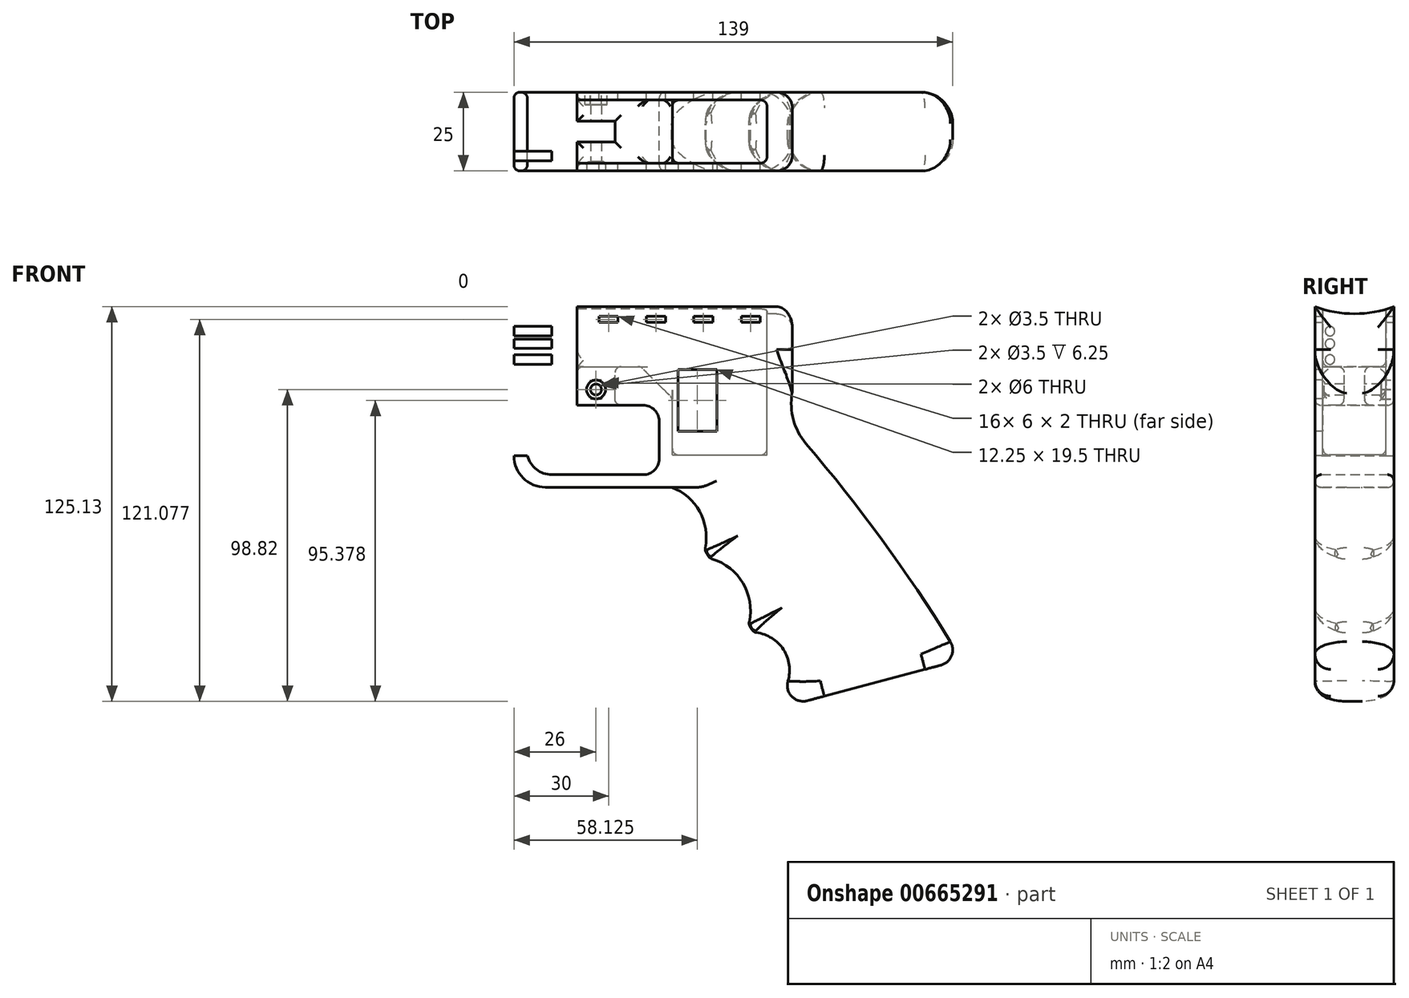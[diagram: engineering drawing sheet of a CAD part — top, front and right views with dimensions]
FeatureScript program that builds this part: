
annotation { "Feature Type Name" : "Feature", "Feature Type Description" : "" }
export const myFeature = defineFeature(function(context is Context, id is Id, definition is map)
    precondition{}
    {
        {
            assignVariable(context, id + "F0", {"name" : "TotalThickness", "anyValue" : 25});
        }
        {
            var Q0;
            Q0=qCreatedBy(makeId("Front.planeOp"),FACE);
            var sketch = newSketch(context, id + "F1", { "sketchPlane" : qUnion([Q0])});
            skLineSegment(sketch, "E0.top", {"start": v(-15, -15) * mm, "end": v(25, -15) * mm});
            skLineSegment(sketch, "E0.left", {"start": v(-25, 10) * mm, "end": v(-25, -5) * mm});
            skPoint(sketch, "E0.middle", {"position": v(0, 0) * mm});
            skLineSegment(sketch, "E1.top", {"start": v(25, 45.26) * mm, "end": v(-25, 45.26) * mm});
            skLineSegment(sketch, "E1.right", {"start": v(-25, 15) * mm, "end": v(-25, 45.26) * mm});
            skPoint(sketch, "E2.visualSharp", {"position": v(-25, -15) * mm});
            skArc(sketch, "E2.filletArc", {"start": v(-25, -5) * mm, "mid": v(-22.07, -12.07) * mm, "end": v(-15, -15) * mm});
            skLineSegment(sketch, "E3.bottom", {"start": v(-21, 11) * mm, "end": v(16, 11) * mm});
            skLineSegment(sketch, "E3.top", {"start": v(-13, -11) * mm, "end": v(16, -11) * mm});
            skLineSegment(sketch, "E3.left", {"start": v(-21, 11) * mm, "end": v(-21, -3) * mm});
            skLineSegment(sketch, "E3.right", {"start": v(21, 6) * mm, "end": v(21, -6) * mm});
            skPoint(sketch, "E4.visualSharp", {"position": v(-21, -11) * mm});
            skArc(sketch, "E4.filletArc", {"start": v(-21, -3) * mm, "mid": v(-18.66, -8.66) * mm, "end": v(-13, -11) * mm});
            skLineSegment(sketch, "E5", {"start": v(-25, 15) * mm, "end": v(-25, 10) * mm});
            skArc(sketch, "E6", {"start": v(60.37, -79.5) * mm, "mid": v(61, -67.48) * mm, "end": v(50.87, -60.96) * mm});
            skLineSegment(sketch, "E7", {"start": v(62.15, -84.17) * mm, "end": v(116.75, -69.64) * mm});
            skArc(sketch, "E8", {"start": v(115.2, -67.07) * mm, "mid": v(92.7, -33.16) * mm, "end": v(67.54, -1.2) * mm});
            skPoint(sketch, "E9.visualSharp", {"position": v(63.17, 15.26) * mm});
            skArc(sketch, "E10", {"start": v(35.45, -34.94) * mm, "mid": v(34, -23) * mm, "end": v(25, -15) * mm});
            skLineSegment(sketch, "E11", {"start": v(35.45, -34.94) * mm, "end": v(37, -37.5) * mm});
            skLineSegment(sketch, "E12", {"start": v(50.87, -60.96) * mm, "end": v(49.35, -58.38) * mm});
            skPoint(sketch, "E13", {"position": v(49.35, -58.38) * mm});
            skArc(sketch, "E14", {"start": v(49.35, -58.38) * mm, "mid": v(47.56, -45.35) * mm, "end": v(37, -37.5) * mm});
            skLineSegment(sketch, "E15", {"start": v(60.37, -79.5) * mm, "end": v(62.15, -84.17) * mm});
            skLineSegment(sketch, "E16", {"start": v(115.2, -67.07) * mm, "end": v(116.75, -69.64) * mm});
            skLineSegment(sketch, "E17.bottom", {"start": v(25, 45.26) * mm, "end": v(63.17, 45.26) * mm});
            skLineSegment(sketch, "E17.right", {"start": v(63.17, 45.26) * mm, "end": v(63.17, 15.26) * mm});
            skLineSegment(sketch, "E18.bottom", {"start": v(-13, 39.26) * mm, "end": v(-7, 39.26) * mm});
            skLineSegment(sketch, "E18.top", {"start": v(-13, 37.26) * mm, "end": v(-7, 37.26) * mm});
            skLineSegment(sketch, "E18.left", {"start": v(-13, 39.26) * mm, "end": v(-13, 37.26) * mm});
            skLineSegment(sketch, "E18.right", {"start": v(-7, 39.26) * mm, "end": v(-7, 37.26) * mm});
            skLineSegment(sketch, "E19.1.0.0", {"start": v(2, 37.26) * mm, "end": v(8, 37.26) * mm});
            skLineSegment(sketch, "E19.1.0.1", {"start": v(8, 39.26) * mm, "end": v(8, 37.26) * mm});
            skLineSegment(sketch, "E19.1.0.2", {"start": v(2, 39.26) * mm, "end": v(8, 39.26) * mm});
            skLineSegment(sketch, "E19.1.0.3", {"start": v(2, 39.26) * mm, "end": v(2, 37.26) * mm});
            skLineSegment(sketch, "E19.2.0.0", {"start": v(17, 37.26) * mm, "end": v(23, 37.26) * mm});
            skLineSegment(sketch, "E19.2.0.1", {"start": v(23, 39.26) * mm, "end": v(23, 37.26) * mm});
            skLineSegment(sketch, "E19.2.0.2", {"start": v(17, 39.26) * mm, "end": v(23, 39.26) * mm});
            skLineSegment(sketch, "E19.2.0.3", {"start": v(17, 39.26) * mm, "end": v(17, 37.26) * mm});
            skLineSegment(sketch, "E19.3.0.0", {"start": v(32, 37.26) * mm, "end": v(38, 37.26) * mm});
            skLineSegment(sketch, "E19.3.0.1", {"start": v(38, 39.26) * mm, "end": v(38, 37.26) * mm});
            skLineSegment(sketch, "E19.3.0.2", {"start": v(32, 39.26) * mm, "end": v(38, 39.26) * mm});
            skLineSegment(sketch, "E19.3.0.3", {"start": v(32, 39.26) * mm, "end": v(32, 37.26) * mm});
            skLineSegment(sketch, "E19.4.0.0", {"start": v(47, 37.26) * mm, "end": v(53, 37.26) * mm});
            skLineSegment(sketch, "E19.4.0.1", {"start": v(53, 39.26) * mm, "end": v(53, 37.26) * mm});
            skLineSegment(sketch, "E19.4.0.2", {"start": v(47, 39.26) * mm, "end": v(53, 39.26) * mm});
            skLineSegment(sketch, "E19.4.0.3", {"start": v(47, 39.26) * mm, "end": v(47, 37.26) * mm});
            skLineSegment(sketch, "E19.direction1", {"start": v(-13, 37.26) * mm, "end": v(2, 37.26) * mm, "construction": true});
            skArc(sketch, "E20", {"start": v(63.17, 15.26) * mm, "mid": v(63.52, 6.55) * mm, "end": v(67.54, -1.2) * mm});
            skPoint(sketch, "E21.visualSharp", {"position": v(21, 11) * mm});
            skArc(sketch, "E21.filletArc", {"start": v(21, 6) * mm, "mid": v(19.54, 9.54) * mm, "end": v(16, 11) * mm});
            skPoint(sketch, "E22.visualSharp", {"position": v(21, -11) * mm});
            skArc(sketch, "E22.filletArc", {"start": v(16, -11) * mm, "mid": v(19.54, -9.54) * mm, "end": v(21, -6) * mm});
            skSolve(sketch);
        }
        {
            var Q0;
            Q0=makeQuery(id+"F1.imprint","IMPRINT",FACE,{"disambiguationData":[TD([[makeQuery(id+"F1.imprint","IMPRINT",EDGE,{"derivedFrom":sQuery(id+"F1.wireOp",EDGE,"E0.top")}),1.0]])]});
            extrude(context, id + "F2", {"entities" : qUnion([Q0]), "depth" : (getVariable(context, 'TotalThickness')) * mm});
        }
        {
            var Q0;
            Q0=makeQuery(id+"FijhAChJVIiYrHk_1.boolean.opBoolean","MERGE",FACE,{"derivedFrom":[makeQuery(id+"F2.opExtrude","SWEPT_FACE",FACE,{"disambiguationData":[OSD([sQuery(id+"F1.wireOp",EDGE,"E1.top")])]}),makeQuery(id+"FijhAChJVIiYrHk_1.opExtrude","CAP_FACE",FACE,{"disambiguationData":[OSD([sQuery(id+"FPGrgiwVji8RH30_1.wireOp",EDGE,"540a66ce-eadd-4f73-87a4-8e37d69b1e98")])],"isStart":false})]});
            var sketch = newSketch(context, id + "F3", { "sketchPlane" : qUnion([Q0])});
            skLineSegment(sketch, "E23.bottom", {"start": v(-13, -2.5) * mm, "end": v(55.17, -2.5) * mm});
            skLineSegment(sketch, "E23.top", {"start": v(-13, -22.5) * mm, "end": v(55.17, -22.5) * mm});
            skLineSegment(sketch, "E23.left", {"start": v(-13, -2.5) * mm, "end": v(-13, -22.5) * mm});
            skLineSegment(sketch, "E23.right", {"start": v(55.17, -2.5) * mm, "end": v(55.17, -22.5) * mm});
            skLineSegment(sketch, "E24", {"start": v(25.17, -2.5) * mm, "end": v(25.17, -22.5) * mm});
            skSolve(sketch);
        }
        {
            var Q0;
            {var subQ0=sQuery(id+"F3.wireOp",EDGE,"E23.right");Q0=makeQuery(id+"F3.imprint","IMPRINT",FACE,{"disambiguationData":[TD([[makeQuery(id+"F3.imprint","IMPRINT",EDGE,{"derivedFrom":subQ0}),-1.0]])]});}
            extrude(context, id + "F4", {"entities" : qUnion([Q0]), "operationType" : NewBodyOperationType.REMOVE, "oppositeDirection" : true, "depth" : 50 * mm});
        }
        {
            var Q0;
            Q0=makeQuery(id+"F3.imprint","IMPRINT",FACE,{"disambiguationData":[TD([[makeQuery(id+"F3.imprint","IMPRINT",EDGE,{"derivedFrom":sQuery(id+"F3.wireOp",EDGE,"E23.bottom")}),-1.0]])]});
            extrude(context, id + "F5", {"entities" : qUnion([Q0]), "operationType" : NewBodyOperationType.REMOVE, "oppositeDirection" : true, "depth" : 22 * mm});
        }
        {
            var Q0;
            Q0=makeQuery(id+"F5.boolean.opBoolean","INTERSECT",EDGE,{"derivedFrom":[makeQuery(id+"F4.boolean.opBoolean","COPY",FACE,{"derivedFrom":makeQuery(id+"F4.opExtrude","SWEPT_FACE",FACE,{"disambiguationData":[OSD([sQuery(id+"F3.wireOp",EDGE,"E24")])]})}),makeQuery(id+"F5.opExtrude","CAP_FACE",FACE,{"disambiguationData":[OSD([sQuery(id+"F3.wireOp",EDGE,"E23.bottom"),sQuery(id+"F3.wireOp",EDGE,"E23.top"),sQuery(id+"F3.wireOp",EDGE,"E23.left"),sQuery(id+"F3.wireOp",EDGE,"E23.right")])],"isStart":false})]});
            chamfer(context, id + "F6", {"entities" : qUnion([Q0]), "width" : 10 * mm, "tangentPropagation" : true});
        }
        {
            var Q0;
            Q0=makeQuery(id+"F2.opExtrude","SWEPT_FACE",FACE,{"disambiguationData":[OSD([sQuery(id+"F1.wireOp",EDGE,"E1.right")])]});
            var sketch = newSketch(context, id + "F7", { "sketchPlane" : qUnion([Q0])});
            skLineSegment(sketch, "E25.bottom", {"start": v(9.25, 18.5) * mm, "end": v(15.75, 18.5) * mm});
            skLineSegment(sketch, "E25.top", {"start": v(9.25, 48.5) * mm, "end": v(15.75, 48.5) * mm});
            skLineSegment(sketch, "E25.left", {"start": v(9.25, 18.5) * mm, "end": v(9.25, 48.5) * mm});
            skLineSegment(sketch, "E25.right", {"start": v(15.75, 18.5) * mm, "end": v(15.75, 48.5) * mm});
            skPoint(sketch, "E25.middle", {"position": v(12.5, 33.5) * mm});
            skSolve(sketch);
        }
        {
            var Q0;
            Q0=makeQuery(id+"F7.imprint","IMPRINT",FACE,{"disambiguationData":[TD([[makeQuery(id+"F7.imprint","IMPRINT",EDGE,{"derivedFrom":sQuery(id+"F7.wireOp",EDGE,"E25.bottom")}),1.0]])]});
            extrude(context, id + "F8", {"entities" : qUnion([Q0]), "operationType" : NewBodyOperationType.REMOVE, "oppositeDirection" : true, "depth" : 20 * mm, "offsetDistance" : 25 * mm});
        }
        {
            var Q0;
            Q0=makeQuery(id+"F5.boolean.opBoolean","COPY",FACE,{"derivedFrom":makeQuery(id+"F5.opExtrude","CAP_FACE",FACE,{"disambiguationData":[OSD([sQuery(id+"F3.wireOp",EDGE,"E23.bottom"),sQuery(id+"F3.wireOp",EDGE,"E23.top"),sQuery(id+"F3.wireOp",EDGE,"E23.left"),sQuery(id+"F3.wireOp",EDGE,"E23.right")])],"isStart":false})});
            var sketch = newSketch(context, id + "F9", { "sketchPlane" : qUnion([Q0])});
            skLineSegment(sketch, "E26.bottom", {"start": v(-5, -9.25) * mm, "end": v(7, -9.25) * mm});
            skLineSegment(sketch, "E26.top", {"start": v(-5, -15.75) * mm, "end": v(7, -15.75) * mm});
            skLineSegment(sketch, "E26.right", {"start": v(7, -9.25) * mm, "end": v(7, -15.75) * mm});
            skLineSegment(sketch, "E27", {"start": v(-5, -9.25) * mm, "end": v(-5, -15.75) * mm});
            skPoint(sketch, "E28", {"position": v(-5, -12.5) * mm});
            skSolve(sketch);
        }
        {
            var Q0;
            Q0=makeQuery(id+"FNvPxtAVWz8euOJ_1.opFillet","SPLIT",FACE,{"disambiguationData":[OD(1.0)],"derivedFrom":makeQuery(id+"F2.opExtrude","CAP_FACE",FACE,{"disambiguationData":[OSD([sQuery(id+"F1.wireOp",EDGE,"E0.bottom"),sQuery(id+"F1.wireOp",EDGE,"E0.top"),sQuery(id+"F1.wireOp",EDGE,"E0.left"),sQuery(id+"F1.wireOp",EDGE,"E0.right"),sQuery(id+"F1.wireOp",EDGE,"E1.bottom"),sQuery(id+"F1.wireOp",EDGE,"E1.top"),sQuery(id+"F1.wireOp",EDGE,"E1.left"),sQuery(id+"F1.wireOp",EDGE,"E1.right"),sQuery(id+"F1.wireOp",EDGE,"E2.filletArc"),sQuery(id+"F1.wireOp",EDGE,"20bca58f-3b4b-4199-85f8-e5d00a776496.filletArc"),sQuery(id+"F1.wireOp",EDGE,"E3.bottom"),sQuery(id+"F1.wireOp",EDGE,"E3.top"),sQuery(id+"F1.wireOp",EDGE,"E3.left"),sQuery(id+"F1.wireOp",EDGE,"E3.right"),sQuery(id+"F1.wireOp",EDGE,"E4.filletArc")])],"isStart":false})});
            var sketch = newSketch(context, id + "F10", { "sketchPlane" : qUnion([Q0])});
            skCircle(sketch, "E29", {"center": v(1, 16) * mm, "radius": 1.75 * mm});
            skCircle(sketch, "E30", {"center": v(1, 16) * mm, "radius": 3 * mm});
            skSolve(sketch);
        }
        {
            var Q0;
            Q0=makeQuery(id+"F10.imprint","IMPRINT",FACE,{"disambiguationData":[TD([[makeQuery(id+"F10.imprint","IMPRINT",EDGE,{"derivedFrom":sQuery(id+"F10.wireOp",EDGE,"E29")}),1.0]])]});
            extrude(context, id + "F11", {"entities" : qUnion([Q0]), "operationType" : NewBodyOperationType.REMOVE, "oppositeDirection" : true, "depth" : (getVariable(context, 'TotalThickness')) * mm});
        }
        {
            var Q0;
            Q0=makeQuery(id+"F10.imprint","IMPRINT",FACE,{"disambiguationData":[TD([[makeQuery(id+"F10.imprint","IMPRINT",EDGE,{"derivedFrom":sQuery(id+"F10.wireOp",EDGE,"E29")}),-1.0]])]});
            extrude(context, id + "F12", {"entities" : qUnion([Q0]), "operationType" : NewBodyOperationType.REMOVE, "oppositeDirection" : true, "depth" : 3 * mm});
        }
        {
            var Q0;
            Q0=makeQuery(id+"F12.boolean.opBoolean","COPY",EDGE,{"derivedFrom":makeQuery(id+"F12.opExtrude","CAP_EDGE",EDGE,{"disambiguationData":[OSD([sQuery(id+"F10.wireOp",EDGE,"E30")])],"isStart":false})});
            var Q1;
            Q1=makeQuery(id+"F12.boolean.opBoolean","COPY",EDGE,{"derivedFrom":makeQuery(id+"F12.opExtrude","CAP_EDGE",EDGE,{"disambiguationData":[OSD([sQuery(id+"F10.wireOp",EDGE,"E30")])],"isStart":true})});
            fillet(context, id + "F13", {"entities" : qUnion([Q0, Q1]), "radius" : 1 * mm, "tangentPropagation" : true, "allowEdgeOverflow" : false});
        }
        {
            var Q0;
            Q0=makeQuery(id+"FNvPxtAVWz8euOJ_1.opFillet","SPLIT",FACE,{"disambiguationData":[OD(0.0)],"derivedFrom":makeQuery(id+"F2.opExtrude","CAP_FACE",FACE,{"disambiguationData":[OSD([sQuery(id+"F1.wireOp",EDGE,"E0.bottom"),sQuery(id+"F1.wireOp",EDGE,"E0.top"),sQuery(id+"F1.wireOp",EDGE,"E0.left"),sQuery(id+"F1.wireOp",EDGE,"E0.right"),sQuery(id+"F1.wireOp",EDGE,"E1.top"),sQuery(id+"F1.wireOp",EDGE,"E1.left"),sQuery(id+"F1.wireOp",EDGE,"E1.right"),sQuery(id+"F1.wireOp",EDGE,"E2.filletArc"),sQuery(id+"F1.wireOp",EDGE,"20bca58f-3b4b-4199-85f8-e5d00a776496.filletArc"),sQuery(id+"F1.wireOp",EDGE,"E3.bottom"),sQuery(id+"F1.wireOp",EDGE,"E3.top"),sQuery(id+"F1.wireOp",EDGE,"E3.left"),sQuery(id+"F1.wireOp",EDGE,"E3.right"),sQuery(id+"F1.wireOp",EDGE,"E4.filletArc")])],"isStart":true})});
            var sketch = newSketch(context, id + "F14", { "sketchPlane" : qUnion([Q0])});
            skCircle(sketch, "E31.cCircle", {"center": v(-1, 16) * mm, "radius": 3 * mm, "construction": true});
            skLineSegment(sketch, "E31.0", {"start": v(-4.46, 15.93) * mm, "end": v(-2.8, 18.96) * mm});
            skLineSegment(sketch, "E31.1", {"start": v(-2.8, 18.96) * mm, "end": v(0.67, 19.03) * mm});
            skLineSegment(sketch, "E31.2", {"start": v(0.67, 19.03) * mm, "end": v(2.46, 16.07) * mm});
            skLineSegment(sketch, "E31.3", {"start": v(2.46, 16.07) * mm, "end": v(0.8, 13.04) * mm});
            skLineSegment(sketch, "E31.4", {"start": v(0.8, 13.04) * mm, "end": v(-2.67, 12.97) * mm});
            skLineSegment(sketch, "E31.5", {"start": v(-2.67, 12.97) * mm, "end": v(-4.46, 15.93) * mm});
            skPoint(sketch, "E31.0.midPoint", {"position": v(-3.63, 17.45) * mm});
            skSolve(sketch);
        }
        {
            var Q0;
            Q0=makeQuery(id+"F14.imprint","IMPRINT",FACE,{"disambiguationData":[TD([[makeQuery(id+"F14.imprint","IMPRINT",EDGE,{"derivedFrom":sQuery(id+"F14.wireOp",EDGE,"E31.0")}),-1.0]])]});
            extrude(context, id + "F15", {"entities" : qUnion([Q0]), "operationType" : NewBodyOperationType.REMOVE, "oppositeDirection" : true, "depth" : 4 * mm});
        }
        {
            var Q0;
            Q0=qCreatedBy(makeId("Right.planeOp"),FACE);
            var sketch = newSketch(context, id + "F16", { "sketchPlane" : qUnion([Q0])});
            skArc(sketch, "E32", {"start": v(-37.25, 50.25) * mm, "mid": v(-12.5, 40) * mm, "end": v(12.25, 50.25) * mm});
            skLineSegment(sketch, "E33", {"start": v(-12.5, 75) * mm, "end": v(-37.25, 50.25) * mm});
            skLineSegment(sketch, "E34", {"start": v(-12.5, 75) * mm, "end": v(12.25, 50.25) * mm});
            skLineSegment(sketch, "E35", {"start": v(-12.5, 75) * mm, "end": v(-12.5, 46.26) * mm});
            skArc(sketch, "E36", {"start": v(-35.48, 52.02) * mm, "mid": v(-12.5, 42.5) * mm, "end": v(10.48, 52.02) * mm});
            skSolve(sketch);
        }
        {
            var Q0;
            {var subQ0=sQuery(id+"F16.wireOp",EDGE,"E32");Q0=makeQuery(id+"F16.imprint","IMPRINT",FACE,{"disambiguationData":[TD([[makeQuery(id+"F16.imprint","IMPRINT",EDGE,{"derivedFrom":subQ0}),1.0]])]});}
            var Q1;
            {var subQ3=sQuery(id+"F16.wireOp",EDGE,"E36");Q1=makeQuery(id+"F16.imprint","IMPRINT",FACE,{"disambiguationData":[TD([[makeQuery(id+"F16.imprint","IMPRINT",EDGE,{"derivedFrom":subQ3}),1.0]])]});}
            extrude(context, id + "F17", {"entities" : qUnion([Q0, Q1]), "operationType" : NewBodyOperationType.REMOVE, "depth" : 70 * mm, "hasSecondDirection" : true, "secondDirectionOppositeDirection" : true, "secondDirectionDepth" : 25 * mm});
        }
        {
            var Q0;
            Q0=makeQuery(id+"F2.opExtrude","SWEPT_FACE",FACE,{"disambiguationData":[OSD([sQuery(id+"F1.wireOp",EDGE,"E0.left"),sQuery(id+"F1.wireOp",EDGE,"E1.right"),sQuery(id+"F1.wireOp",EDGE,"E5")])]});
            var sketch = newSketch(context, id + "F18", { "sketchPlane" : qUnion([Q0])});
            skCircle(sketch, "E37", {"center": v(4.75, 34.5) * mm, "radius": 1.5 * mm});
            skCircle(sketch, "E38", {"center": v(4.75, 30.5) * mm, "radius": 1.5 * mm});
            skCircle(sketch, "E39", {"center": v(4.75, 25.5) * mm, "radius": 1.5 * mm});
            skLineSegment(sketch, "E40", {"start": v(12.5, 18.5) * mm, "end": v(12.5, 39.93) * mm, "construction": true});
            skPoint(sketch, "E40.endSnap0", {"position": v(12.5, 18.5) * mm});
            skCircle(sketch, "E41.MirrorC", {"center": v(20.25, 34.5) * mm, "radius": 1.5 * mm});
            skCircle(sketch, "E42.MirrorC", {"center": v(20.25, 30.5) * mm, "radius": 1.5 * mm});
            skCircle(sketch, "E43.MirrorC", {"center": v(20.25, 25.5) * mm, "radius": 1.5 * mm});
            skSolve(sketch);
        }
        {
            var Q0;
            Q0=makeQuery(id+"F18.imprint","IMPRINT",FACE,{"disambiguationData":[TD([[makeQuery(id+"F18.imprint","IMPRINT",EDGE,{"derivedFrom":sQuery(id+"F18.wireOp",EDGE,"E37")}),1.0]])]});
            var Q1;
            Q1=makeQuery(id+"F18.imprint","IMPRINT",FACE,{"disambiguationData":[TD([[makeQuery(id+"F18.imprint","IMPRINT",EDGE,{"derivedFrom":sQuery(id+"F18.wireOp",EDGE,"E38")}),1.0]])]});
            var Q2;
            Q2=makeQuery(id+"F18.imprint","IMPRINT",FACE,{"disambiguationData":[TD([[makeQuery(id+"F18.imprint","IMPRINT",EDGE,{"derivedFrom":sQuery(id+"F18.wireOp",EDGE,"E39")}),1.0]])]});
            var Q3;
            Q3=makeQuery(id+"F18.imprint","IMPRINT",FACE,{"disambiguationData":[TD([[makeQuery(id+"F18.imprint","IMPRINT",EDGE,{"derivedFrom":sQuery(id+"F18.wireOp",EDGE,"E38")}),1.0]])]});
            var Q4;
            Q4=makeQuery(id+"F18.imprint","IMPRINT",FACE,{"disambiguationData":[TD([[makeQuery(id+"F18.imprint","IMPRINT",EDGE,{"derivedFrom":sQuery(id+"F18.wireOp",EDGE,"E43.MirrorC")}),-1.0]])]});
            var Q5;
            Q5=makeQuery(id+"F18.imprint","IMPRINT",FACE,{"disambiguationData":[TD([[makeQuery(id+"F18.imprint","IMPRINT",EDGE,{"derivedFrom":sQuery(id+"F18.wireOp",EDGE,"E42.MirrorC")}),-1.0]])]});
            var Q6;
            Q6=makeQuery(id+"F18.imprint","IMPRINT",FACE,{"disambiguationData":[TD([[makeQuery(id+"F18.imprint","IMPRINT",EDGE,{"derivedFrom":sQuery(id+"F18.wireOp",EDGE,"E41.MirrorC")}),-1.0]])]});
            extrude(context, id + "F19", {"entities" : qUnion([Q0, Q1, Q2, Q3, Q4, Q5, Q6]), "operationType" : NewBodyOperationType.REMOVE, "oppositeDirection" : true, "depth" : 20 * mm, "offsetDistance" : 25 * mm});
        }
        {
            var Q0;
            Q0=makeQuery(id+"F9.imprint","IMPRINT",FACE,{"disambiguationData":[TD([[makeQuery(id+"F9.imprint","IMPRINT",EDGE,{"derivedFrom":sQuery(id+"F9.wireOp",EDGE,"E26.bottom")}),-1.0]])]});
            extrude(context, id + "F20", {"entities" : qUnion([Q0]), "operationType" : NewBodyOperationType.REMOVE, "oppositeDirection" : true, "depth" : 25 * mm});
        }
        {
            var Q0;
            Q0=makeQuery(id+"F2.opExtrude","CAP_EDGE",EDGE,{"disambiguationData":[OSD([sQuery(id+"F1.wireOp",EDGE,"E6")])],"isStart":true});
            var Q1;
            Q1=makeQuery(id+"F2.opExtrude","CAP_EDGE",EDGE,{"disambiguationData":[OSD([sQuery(id+"F1.wireOp",EDGE,"E14")])],"isStart":true});
            var Q2;
            Q2=makeQuery(id+"F2.opExtrude","CAP_EDGE",EDGE,{"disambiguationData":[OSD([sQuery(id+"F1.wireOp",EDGE,"E10")])],"isStart":true});
            var Q3;
            Q3=makeQuery(id+"F2.opExtrude","CAP_EDGE",EDGE,{"disambiguationData":[OSD([sQuery(id+"F1.wireOp",EDGE,"E10")])],"isStart":false});
            var Q4;
            Q4=makeQuery(id+"F2.opExtrude","CAP_EDGE",EDGE,{"disambiguationData":[OSD([sQuery(id+"F1.wireOp",EDGE,"E14")])],"isStart":false});
            var Q5;
            Q5=makeQuery(id+"F2.opExtrude","CAP_EDGE",EDGE,{"disambiguationData":[OSD([sQuery(id+"F1.wireOp",EDGE,"E6")])],"isStart":false});
            var Q6;
            Q6=makeQuery(id+"F2.opExtrude","CAP_EDGE",EDGE,{"disambiguationData":[OSD([sQuery(id+"F1.wireOp",EDGE,"E8")])],"isStart":true});
            var Q7;
            Q7=makeQuery(id+"F2.opExtrude","CAP_EDGE",EDGE,{"disambiguationData":[OSD([sQuery(id+"F1.wireOp",EDGE,"E8")])],"isStart":false});
            fillet(context, id + "F21", {"entities" : qUnion([Q0, Q1, Q2, Q3, Q4, Q5, Q6, Q7]), "radius" : 10 * mm, "tangentPropagation" : true, "allowEdgeOverflow" : false});
        }
        {
            var Q0;
            Q0=makeQuery(id+"F2.opExtrude","CAP_EDGE",EDGE,{"disambiguationData":[OSD([sQuery(id+"F1.wireOp",EDGE,"E7")])],"isStart":true});
            var Q1;
            Q1=makeQuery(id+"F2.opExtrude","SWEPT_EDGE",EDGE,{"disambiguationData":[OSD([sQuery(id+"F1.wireOp",EDGE,"E7"),sQuery(id+"F1.wireOp",EDGE,"E15")])]});
            var Q2;
            Q2=makeQuery(id+"F17.boolean.opBoolean","INTERSECT",EDGE,{"derivedFrom":[makeQuery(id+"F2.opExtrude","SWEPT_FACE",FACE,{"disambiguationData":[OSD([sQuery(id+"F1.wireOp",EDGE,"E17.right")])]}),makeQuery(id+"F17.opExtrude","SWEPT_FACE",FACE,{"disambiguationData":[OSD([sQuery(id+"F16.wireOp",EDGE,"E32")])]})]});
            var Q3;
            Q3=makeQuery(id+"F2.opExtrude","CAP_EDGE",EDGE,{"disambiguationData":[OSD([sQuery(id+"F1.wireOp",EDGE,"E17.right")])],"isStart":false});
            fillet(context, id + "F22", {"entities" : qUnion([Q0, Q1, Q2, Q3]), "radius" : 5 * mm, "tangentPropagation" : true, "allowEdgeOverflow" : false});
        }
        {
            var Q0;
            Q0=makeQuery(id+"F2.opExtrude","CAP_EDGE",EDGE,{"disambiguationData":[OSD([sQuery(id+"F1.wireOp",EDGE,"E3.top")])],"isStart":false});
            var Q1;
            Q1=makeQuery(id+"F2.opExtrude","CAP_EDGE",EDGE,{"disambiguationData":[OSD([sQuery(id+"F1.wireOp",EDGE,"E0.top")])],"isStart":true});
            var Q2;
            Q2=makeQuery(id+"F2.opExtrude","CAP_EDGE",EDGE,{"disambiguationData":[OSD([sQuery(id+"F1.wireOp",EDGE,"E0.top")])],"isStart":false});
            var Q3;
            Q3=makeQuery(id+"F2.opExtrude","CAP_EDGE",EDGE,{"disambiguationData":[OSD([sQuery(id+"F1.wireOp",EDGE,"E3.top")])],"isStart":true});
            var Q4;
            Q4=makeQuery(id+"F2.opExtrude","CAP_EDGE",EDGE,{"disambiguationData":[OSD([sQuery(id+"F1.wireOp",EDGE,"E3.right")])],"isStart":true});
            var Q5;
            Q5=makeQuery(id+"F2.opExtrude","CAP_EDGE",EDGE,{"disambiguationData":[OSD([sQuery(id+"F1.wireOp",EDGE,"E3.left")])],"isStart":true});
            var Q6;
            Q6=makeQuery(id+"F2.opExtrude","CAP_EDGE",EDGE,{"disambiguationData":[OSD([sQuery(id+"F1.wireOp",EDGE,"E3.right")])],"isStart":false});
            var Q7;
            Q7=makeQuery(id+"F2.opExtrude","CAP_EDGE",EDGE,{"disambiguationData":[OSD([sQuery(id+"F1.wireOp",EDGE,"E3.bottom")])],"isStart":true});
            var Q8;
            Q8=makeQuery(id+"F2.opExtrude","CAP_EDGE",EDGE,{"disambiguationData":[OSD([sQuery(id+"F1.wireOp",EDGE,"E3.bottom")])],"isStart":false});
            var Q9;
            Q9=makeQuery(id+"F2.opExtrude","SWEPT_EDGE",EDGE,{"disambiguationData":[OSD([sQuery(id+"F1.wireOp",EDGE,"E3.top"),sQuery(id+"F1.wireOp",EDGE,"E3.right")])]});
            var Q10;
            Q10=makeQuery(id+"F2.opExtrude","SWEPT_EDGE",EDGE,{"disambiguationData":[OSD([sQuery(id+"F1.wireOp",EDGE,"E3.bottom"),sQuery(id+"F1.wireOp",EDGE,"E3.left")])]});
            var Q11;
            Q11=makeQuery(id+"F2.opExtrude","SWEPT_EDGE",EDGE,{"disambiguationData":[OSD([sQuery(id+"F1.wireOp",EDGE,"E3.bottom"),sQuery(id+"F1.wireOp",EDGE,"E3.right")])]});
            var Q12;
            Q12=makeQuery(id+"F20.boolean.opBoolean","INTERSECT",EDGE,{"derivedFrom":[makeQuery(id+"F2.opExtrude","SWEPT_FACE",FACE,{"disambiguationData":[OSD([sQuery(id+"F1.wireOp",EDGE,"E3.bottom")])]}),makeQuery(id+"F20.opExtrude","SWEPT_FACE",FACE,{"disambiguationData":[OSD([sQuery(id+"F9.wireOp",EDGE,"E26.top")])]})]});
            var Q13;
            Q13=makeQuery(id+"F20.boolean.opBoolean","INTERSECT",EDGE,{"derivedFrom":[makeQuery(id+"F2.opExtrude","SWEPT_FACE",FACE,{"disambiguationData":[OSD([sQuery(id+"F1.wireOp",EDGE,"E3.bottom")])]}),makeQuery(id+"F20.opExtrude","SWEPT_FACE",FACE,{"disambiguationData":[OSD([sQuery(id+"F9.wireOp",EDGE,"E26.right")])]})]});
            var Q14;
            Q14=makeQuery(id+"F20.boolean.opBoolean","INTERSECT",EDGE,{"derivedFrom":[makeQuery(id+"F2.opExtrude","SWEPT_FACE",FACE,{"disambiguationData":[OSD([sQuery(id+"F1.wireOp",EDGE,"E3.bottom")])]}),makeQuery(id+"F20.opExtrude","SWEPT_FACE",FACE,{"disambiguationData":[OSD([sQuery(id+"F9.wireOp",EDGE,"E26.bottom")])]})]});
            var Q15;
            Q15=makeQuery(id+"F20.boolean.opBoolean","INTERSECT",EDGE,{"derivedFrom":[makeQuery(id+"F2.opExtrude","SWEPT_FACE",FACE,{"disambiguationData":[OSD([sQuery(id+"F1.wireOp",EDGE,"E3.bottom")])]}),makeQuery(id+"F20.opExtrude","SWEPT_FACE",FACE,{"disambiguationData":[OSD([sQuery(id+"F9.wireOp",EDGE,"E27")])]})]});
            var Q16;
            Q16=makeQuery(id+"F8.boolean.opBoolean","COPY",FACE,{"derivedFrom":makeQuery(id+"F8.opExtrude","SWEPT_FACE",FACE,{"disambiguationData":[OSD([sQuery(id+"F7.wireOp",EDGE,"E25.bottom")])]})});
            var Q17;
            Q17=makeQuery(id+"F5.boolean.opBoolean","COPY",EDGE,{"derivedFrom":makeQuery(id+"F5.opExtrude","SWEPT_EDGE",EDGE,{"disambiguationData":[OSD([sQuery(id+"F3.wireOp",EDGE,"E23.top"),sQuery(id+"F3.wireOp",EDGE,"E23.right")])]})});
            var Q18;
            Q18=makeQuery(id+"F5.boolean.opBoolean","COPY",EDGE,{"derivedFrom":makeQuery(id+"F5.opExtrude","SWEPT_EDGE",EDGE,{"disambiguationData":[OSD([sQuery(id+"F3.wireOp",EDGE,"E23.bottom"),sQuery(id+"F3.wireOp",EDGE,"E23.right")])]})});
            var Q19;
            Q19=makeQuery(id+"F2.opExtrude","SWEPT_FACE",FACE,{"disambiguationData":[OSD([sQuery(id+"F1.wireOp",EDGE,"E11")])]});
            var Q20;
            Q20=makeQuery(id+"F2.opExtrude","SWEPT_FACE",FACE,{"disambiguationData":[OSD([sQuery(id+"F1.wireOp",EDGE,"E12")])]});
            var Q21;
            Q21=makeQuery(id+"F21.opFillet","BLEND_EDGE",EDGE,{"blendedFrom":[makeQuery(id+"F2.opExtrude","CAP_EDGE",EDGE,{"disambiguationData":[OSD([sQuery(id+"F1.wireOp",EDGE,"E10")])],"isStart":true}),makeQuery(id+"F2.opExtrude","CAP_EDGE",EDGE,{"disambiguationData":[OSD([sQuery(id+"F1.wireOp",EDGE,"E14")])],"isStart":true})],"blendedInto":[]});
            var Q22;
            Q22=makeQuery(id+"F21.opFillet","BLEND_EDGE",EDGE,{"blendedFrom":[makeQuery(id+"F2.opExtrude","CAP_EDGE",EDGE,{"disambiguationData":[OSD([sQuery(id+"F1.wireOp",EDGE,"E10")])],"isStart":false}),makeQuery(id+"F2.opExtrude","CAP_EDGE",EDGE,{"disambiguationData":[OSD([sQuery(id+"F1.wireOp",EDGE,"E14")])],"isStart":false})],"blendedInto":[]});
            var Q23;
            Q23=makeQuery(id+"F21.opFillet","BLEND_EDGE",EDGE,{"blendedFrom":[makeQuery(id+"F2.opExtrude","CAP_EDGE",EDGE,{"disambiguationData":[OSD([sQuery(id+"F1.wireOp",EDGE,"E6")])],"isStart":false}),makeQuery(id+"F2.opExtrude","CAP_EDGE",EDGE,{"disambiguationData":[OSD([sQuery(id+"F1.wireOp",EDGE,"E14")])],"isStart":false})],"blendedInto":[]});
            var Q24;
            Q24=makeQuery(id+"F21.opFillet","BLEND_EDGE",EDGE,{"blendedFrom":[makeQuery(id+"F2.opExtrude","CAP_EDGE",EDGE,{"disambiguationData":[OSD([sQuery(id+"F1.wireOp",EDGE,"E6")])],"isStart":true}),makeQuery(id+"F2.opExtrude","CAP_EDGE",EDGE,{"disambiguationData":[OSD([sQuery(id+"F1.wireOp",EDGE,"E14")])],"isStart":true})],"blendedInto":[]});
            var Q25;
            Q25=makeQuery(id+"F5.boolean.opBoolean","COPY",FACE,{"derivedFrom":makeQuery(id+"F5.opExtrude","CAP_FACE",FACE,{"disambiguationData":[OSD([sQuery(id+"F3.wireOp",EDGE,"E23.bottom"),sQuery(id+"F3.wireOp",EDGE,"E23.top"),sQuery(id+"F3.wireOp",EDGE,"E23.left"),sQuery(id+"F3.wireOp",EDGE,"E23.right")])],"isStart":false})});
            var Q26;
            Q26=makeQuery(id+"F4.boolean.opBoolean","COPY",FACE,{"derivedFrom":makeQuery(id+"F4.opExtrude","CAP_FACE",FACE,{"disambiguationData":[OSD([sQuery(id+"F3.wireOp",EDGE,"E23.bottom"),sQuery(id+"F3.wireOp",EDGE,"E23.top"),sQuery(id+"F3.wireOp",EDGE,"E23.right"),sQuery(id+"F3.wireOp",EDGE,"E24")])],"isStart":false})});
            var Q27;
            Q27=makeQuery(id+"F4.boolean.opBoolean","COPY",FACE,{"derivedFrom":makeQuery(id+"F4.opExtrude","SWEPT_FACE",FACE,{"disambiguationData":[OSD([sQuery(id+"F3.wireOp",EDGE,"E24")])]})});
            var Q28;
            Q28=makeQuery(id+"F4.boolean.opBoolean","COPY",EDGE,{"derivedFrom":makeQuery(id+"F4.opExtrude","SWEPT_EDGE",EDGE,{"disambiguationData":[OSD([sQuery(id+"F3.wireOp",EDGE,"E23.bottom"),sQuery(id+"F3.wireOp",EDGE,"E23.right")])]})});
            var Q29;
            Q29=makeQuery(id+"F4.boolean.opBoolean","COPY",EDGE,{"derivedFrom":makeQuery(id+"F4.opExtrude","SWEPT_EDGE",EDGE,{"disambiguationData":[OSD([sQuery(id+"F3.wireOp",EDGE,"E23.top"),sQuery(id+"F3.wireOp",EDGE,"E23.right")])]})});
            fillet(context, id + "F23", {"entities" : qUnion([Q0, Q1, Q2, Q3, Q4, Q5, Q6, Q7, Q8, Q9, Q10, Q11, Q12, Q13, Q14, Q15, Q16, Q17, Q18, Q19, Q20, Q21, Q22, Q23, Q24, Q25, Q26, Q27, Q28, Q29]), "radius" : 2 * mm, "tangentPropagation" : true, "allowEdgeOverflow" : false});
        }
        {
            var Q0;
            Q0=makeQuery(id+"F23.opFillet","SPLIT",FACE,{"disambiguationData":[OD(1.0)],"derivedFrom":makeQuery(id+"F2.opExtrude","CAP_FACE",FACE,{"disambiguationData":[OSD([sQuery(id+"F1.wireOp",EDGE,"E0.top"),sQuery(id+"F1.wireOp",EDGE,"E0.left"),sQuery(id+"F1.wireOp",EDGE,"E1.top"),sQuery(id+"F1.wireOp",EDGE,"E1.right"),sQuery(id+"F1.wireOp",EDGE,"E2.filletArc"),sQuery(id+"F1.wireOp",EDGE,"E3.bottom"),sQuery(id+"F1.wireOp",EDGE,"E3.top"),sQuery(id+"F1.wireOp",EDGE,"E3.left"),sQuery(id+"F1.wireOp",EDGE,"E3.right"),sQuery(id+"F1.wireOp",EDGE,"E4.filletArc"),sQuery(id+"F1.wireOp",EDGE,"E5"),sQuery(id+"F1.wireOp",EDGE,"gKzmcJLQ-WiJM-RmXf-eO38-Hl26mKQAXSxK"),sQuery(id+"F1.wireOp",EDGE,"4uFAXKKD-Hbey-MXQH-G550-3fq9gBtEBOO4"),sQuery(id+"F1.wireOp",EDGE,"E6"),sQuery(id+"F1.wireOp",EDGE,"E7"),sQuery(id+"F1.wireOp",EDGE,"E8"),sQuery(id+"F1.wireOp",EDGE,"E10"),sQuery(id+"F1.wireOp",EDGE,"E11"),sQuery(id+"F1.wireOp",EDGE,"E12"),sQuery(id+"F1.wireOp",EDGE,"E14"),sQuery(id+"F1.wireOp",EDGE,"E15"),sQuery(id+"F1.wireOp",EDGE,"E16"),sQuery(id+"F1.wireOp",EDGE,"E17.bottom"),sQuery(id+"F1.wireOp",EDGE,"E17.right"),sQuery(id+"F1.wireOp",EDGE,"E18.bottom"),sQuery(id+"F1.wireOp",EDGE,"E18.top"),sQuery(id+"F1.wireOp",EDGE,"E18.left"),sQuery(id+"F1.wireOp",EDGE,"E18.right"),sQuery(id+"F1.wireOp",EDGE,"E19.1.0.0"),sQuery(id+"F1.wireOp",EDGE,"E19.1.0.1"),sQuery(id+"F1.wireOp",EDGE,"E19.1.0.2"),sQuery(id+"F1.wireOp",EDGE,"E19.1.0.3"),sQuery(id+"F1.wireOp",EDGE,"E19.2.0.0"),sQuery(id+"F1.wireOp",EDGE,"E19.2.0.1"),sQuery(id+"F1.wireOp",EDGE,"E19.2.0.2"),sQuery(id+"F1.wireOp",EDGE,"E19.2.0.3"),sQuery(id+"F1.wireOp",EDGE,"E19.3.0.0"),sQuery(id+"F1.wireOp",EDGE,"E19.3.0.1"),sQuery(id+"F1.wireOp",EDGE,"E19.3.0.2"),sQuery(id+"F1.wireOp",EDGE,"E19.3.0.3"),sQuery(id+"F1.wireOp",EDGE,"E19.4.0.0"),sQuery(id+"F1.wireOp",EDGE,"E19.4.0.1"),sQuery(id+"F1.wireOp",EDGE,"E19.4.0.2"),sQuery(id+"F1.wireOp",EDGE,"E19.4.0.3"),sQuery(id+"F1.wireOp",EDGE,"E20"),sQuery(id+"F1.wireOp",EDGE,"E21.filletArc"),sQuery(id+"F1.wireOp",EDGE,"E22.filletArc")])],"isStart":false})});
            var sketch = newSketch(context, id + "F24", { "sketchPlane" : qUnion([Q0])});
            skLineSegment(sketch, "E44.bottom", {"start": v(27, 22.3) * mm, "end": v(39.25, 22.3) * mm});
            skLineSegment(sketch, "E44.top", {"start": v(27, 2.8) * mm, "end": v(39.25, 2.8) * mm});
            skLineSegment(sketch, "E44.left", {"start": v(27, 22.3) * mm, "end": v(27, 2.8) * mm});
            skLineSegment(sketch, "E44.right", {"start": v(39.25, 22.3) * mm, "end": v(39.25, 2.8) * mm});
            skSolve(sketch);
        }
        {
            var Q0;
            Q0=makeQuery(id+"F24.imprint","IMPRINT",FACE,{"disambiguationData":[TD([[makeQuery(id+"F24.imprint","IMPRINT",EDGE,{"derivedFrom":sQuery(id+"F24.wireOp",EDGE,"E44.bottom")}),-1.0]])]});
            var Q1;
            {var subQ0=sQuery(id+"F3.wireOp",EDGE,"E23.top");Q1=makeQuery(id+"F5.boolean.opBoolean","MERGE",FACE,{"derivedFrom":[makeQuery(id+"F4.boolean.opBoolean","COPY",FACE,{"derivedFrom":makeQuery(id+"F4.opExtrude","SWEPT_FACE",FACE,{"disambiguationData":[OSD([subQ0])]})}),makeQuery(id+"F5.opExtrude","SWEPT_FACE",FACE,{"disambiguationData":[OSD([subQ0])]})]});}
            extrude(context, id + "F25", {"entities" : qUnion([Q0]), "operationType" : NewBodyOperationType.REMOVE, "endBound" : BoundingType.UP_TO_SURFACE, "oppositeDirection" : true, "endBoundEntityFace" : qUnion([Q1]), "depth" : 5 * mm, "offsetDistance" : 25 * mm});
        }
    });
